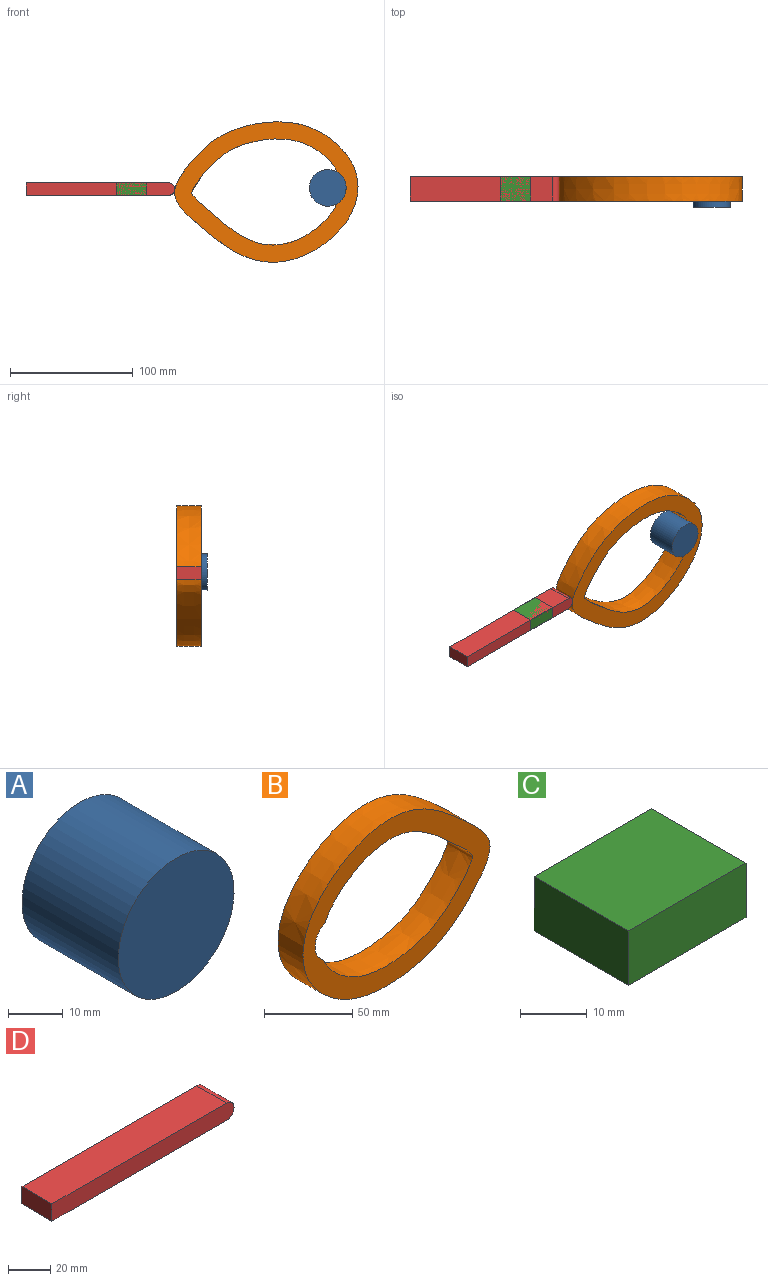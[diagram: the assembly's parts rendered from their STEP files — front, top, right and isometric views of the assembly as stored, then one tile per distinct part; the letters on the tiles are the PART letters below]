
ASSEMBLY  parts=4 mates=2
PART A: 3 faces, bbox 30x25x30 mm
  f0: cylinder r=15mm len=30mm, axis (0,1,0), area 2356.2mm2, adj f1,f2
  f1: plane 30x30mm, normal (0,-1,0), area 706.9mm2, adj f0
  f2: plane 30x30mm, normal (0,1,0), area 706.9mm2, adj f0
PART B: 5 faces, bbox 151.5x20x116.2 mm
  f0: plane 151.47x116.19mm, normal (0,1,0), area 5005mm2, adj f2,f3,f4
  f1: plane 151.47x116.19mm, normal (0,-1,0), area 5005mm2, adj f2,f3,f4
  f2: extruded ~119.34x86.25mm, area 5891.8mm2, adj f0,f1,f4
  f3: extruded ~149.72x114.2mm, area 8159.9mm2, adj f0,f1
  f4: cylinder r=15mm len=25.72mm, axis (0,1,0), area 619.2mm2, adj f0,f1,f2
PART C: 6 faces, bbox 25x20x10 mm
  f0: plane 25x10mm, normal (0,-1,0), area 250mm2, adj f1,f3,f4,f5
  f1: plane 25x20mm, normal (0,0,1), area 500mm2, adj f0,f2,f4,f5
  f2: plane 25x10mm, normal (0,1,0), area 250mm2, adj f1,f3,f4,f5
  f3: plane 25x20mm, normal (0,0,-1), area 500mm2, adj f0,f2,f4,f5
  f4: plane 20x10mm, normal (-1,0,0), area 200mm2, adj f0,f1,f2,f3
  f5: plane 20x10mm, normal (1,0,0), area 200mm2, adj f0,f1,f2,f3
PART D: 6 faces, bbox 121.6x20x10 mm
  f0: plane 116.55x20mm, normal (0,0,-1), area 2331mm2, adj f1,f3,f4,f5
  f1: cylinder r=5mm len=20mm, axis (0,-1,0), area 314.2mm2, adj f0,f2,f4,f5
  f2: plane 116.55x20mm, normal (0,0,1), area 2331mm2, adj f1,f3,f4,f5
  f3: plane 20x10mm, normal (-1,0,0), area 200mm2, adj f0,f2,f4,f5
  f4: plane 121.55x10mm, normal (0,1,0), area 1204.8mm2, adj f0,f1,f2,f3
  f5: plane 121.55x10mm, normal (0,-1,0), area 1204.8mm2, adj f0,f1,f2,f3
PLACE A t=(94.52,-60.3,-110.46)mm fixed
PLACE B rot(axis=(0,1,0),177.8deg) t=(-4.99,-12.7,-112.38)mm
PLACE C t=(93.46,-60.18,-111.44)mm fixed
PLACE D t=(-5.04,-60.18,-111.44)mm
MATE revolute A.f0 <-> B.f4  axis (0,1,0) through (44.75,-60.3,-110.46)mm
MATE slider C.f5 <-> D.f3  axis (1,0,0) through (-102.97,-70.18,-111.44)mm
